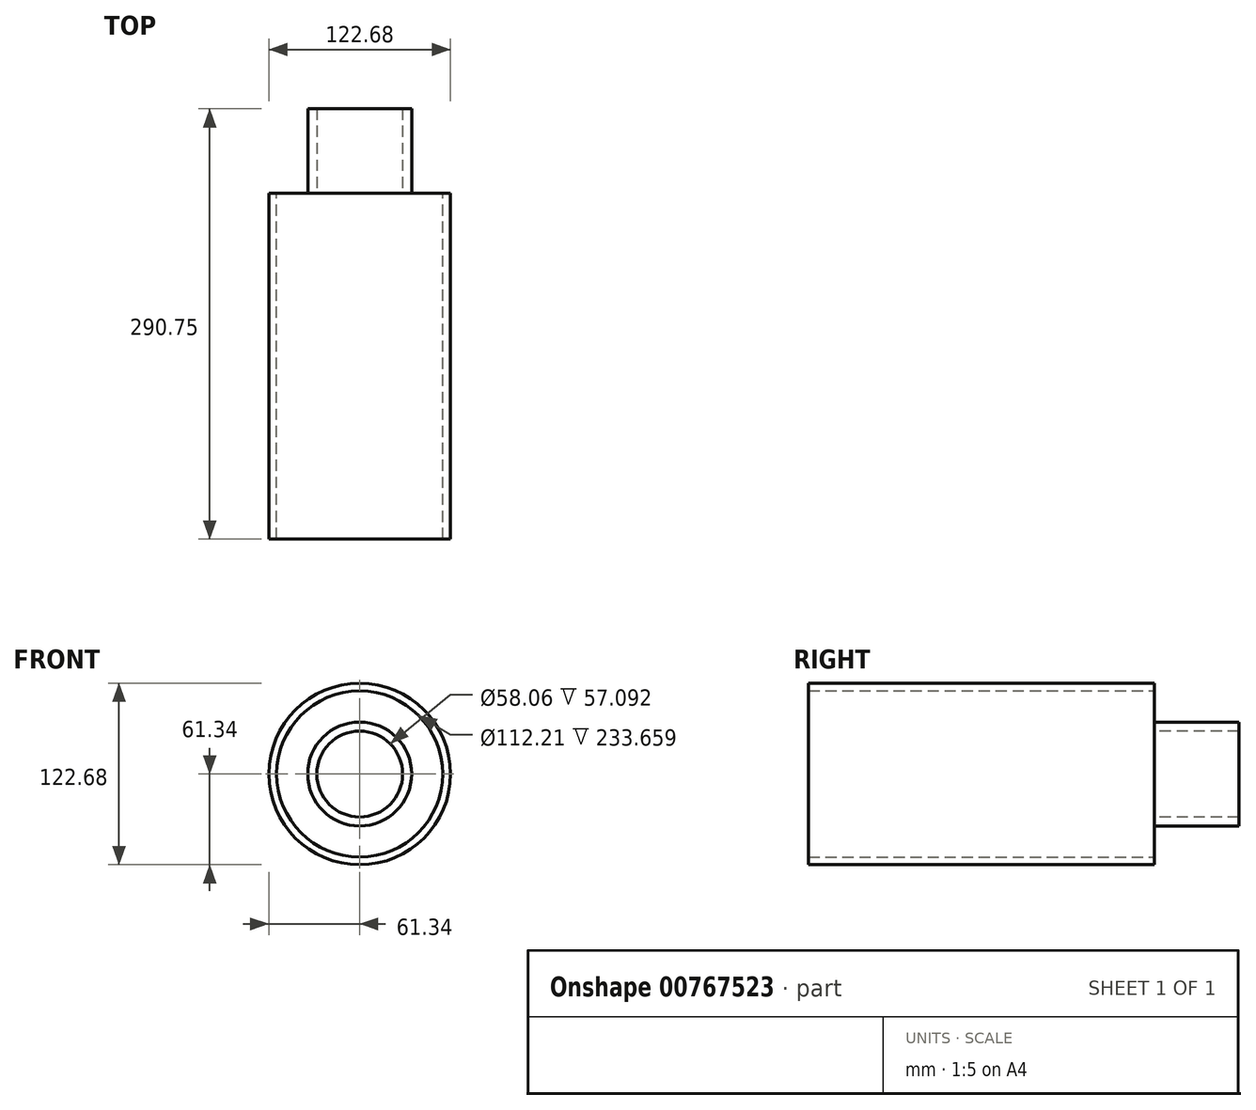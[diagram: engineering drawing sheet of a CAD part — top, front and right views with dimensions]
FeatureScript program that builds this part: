
annotation { "Feature Type Name" : "Feature", "Feature Type Description" : "" }
export const myFeature = defineFeature(function(context is Context, id is Id, definition is map)
    precondition{}
    {
        {
            var Q0;
            Q0=qCreatedBy(makeId("Front.planeOp"),FACE);
            var sketch = newSketch(context, id + "F0", { "sketchPlane" : qUnion([Q0])});
            skCircle(sketch, "E0", {"center": v(0, 0) * mm, "radius": 61.34 * mm});
            skCircle(sketch, "E1", {"center": v(0, 0) * mm, "radius": 56.1 * mm});
            skSolve(sketch);
        }
        {
            var Q0;
            Q0 = qSketchRegion(id + "F0", true);
            extrude(context, id + "F1", {"entities" : qUnion([Q0]), "depth" : 233.66 * mm, "offsetDistance" : 25.4 * mm});
        }
        {
            var Q0;
            Q0=qCreatedBy(makeId("Front.planeOp"),FACE);
            var sketch = newSketch(context, id + "F2", { "sketchPlane" : qUnion([Q0])});
            skCircle(sketch, "E2", {"center": v(0, 0) * mm, "radius": 29.03 * mm});
            skCircle(sketch, "E3", {"center": v(0, 0) * mm, "radius": 35.12 * mm});
            skSolve(sketch);
        }
        {
            var Q0;
            Q0 = qSketchRegion(id + "F2", true);
            extrude(context, id + "F3", {"entities" : qUnion([Q0]), "oppositeDirection" : true, "depth" : 57.1 * mm, "offsetDistance" : 25.4 * mm});
        }
    });
